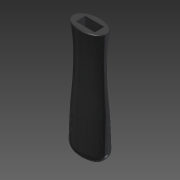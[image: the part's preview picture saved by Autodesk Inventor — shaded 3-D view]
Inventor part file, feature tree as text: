
AUTODESK INVENTOR PART (.ipt)
format: ipt  version: 2015 (Build 190159000, 159)  size: 335,360 bytes
history: native  units: mm
features: sketch x6, other x4, fillet x2, loft x1, extrude x1
ambient origin geometry x8: Origin, YZ Plane, XZ Plane, XY Plane, X Axis, Y Axis, Z Axis, Center Point
bodies: Body1 (feature_tree)
feature tree (14):
  sketch  "Szkic1"
  other  "Płaszczyzna konstrukcyjna1"
  sketch  "Szkic4"
  other  "Płaszczyzna konstrukcyjna2"
  sketch  "Szkic5"
  other  "Płaszczyzna konstrukcyjna3"
  sketch  "Szkic6"
  other  "Płaszczyzna konstrukcyjna4"
  loft  "Wyciągnięcie złożone2"
  fillet  "Zaokrąglenie1"  Radius=5.0mm
  fillet  "Zaokrąglenie2"  Radius=9.0mm
  extrude  "Wyciągnięcie proste1"  Depth=5.5mm
  sketch  "Szkic7"
  sketch  "Szkic8"
